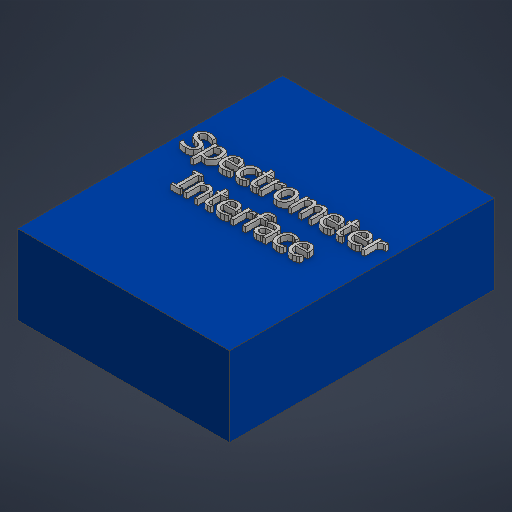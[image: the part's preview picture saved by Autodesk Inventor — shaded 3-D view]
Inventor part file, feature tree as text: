
AUTODESK INVENTOR PART (.ipt)
format: ipt  version: 2025.1 (Build 291241000, 241)  size: 704,512 bytes
history: native  units: mm
features: extrude x2, sketch x2
ambient origin geometry x8: Origin, YZ Plane, XZ Plane, XY Plane, X Axis, Y Axis, Z Axis, Center Point
bodies: Solid1 (feature_tree)
feature tree (4):
  extrude  "Extrusion1"  Depth=100.0mm
  extrude  "Extrusion2"  Depth=2.0mm TaperAngle=0.0deg
  sketch  "Sketch1"  dims[d0=80.0mm d1=100.0mm]
  sketch  "Sketch2"  dims[d2=30.0mm d3=0.0mm d4=2.0mm d5=0.0mm]
